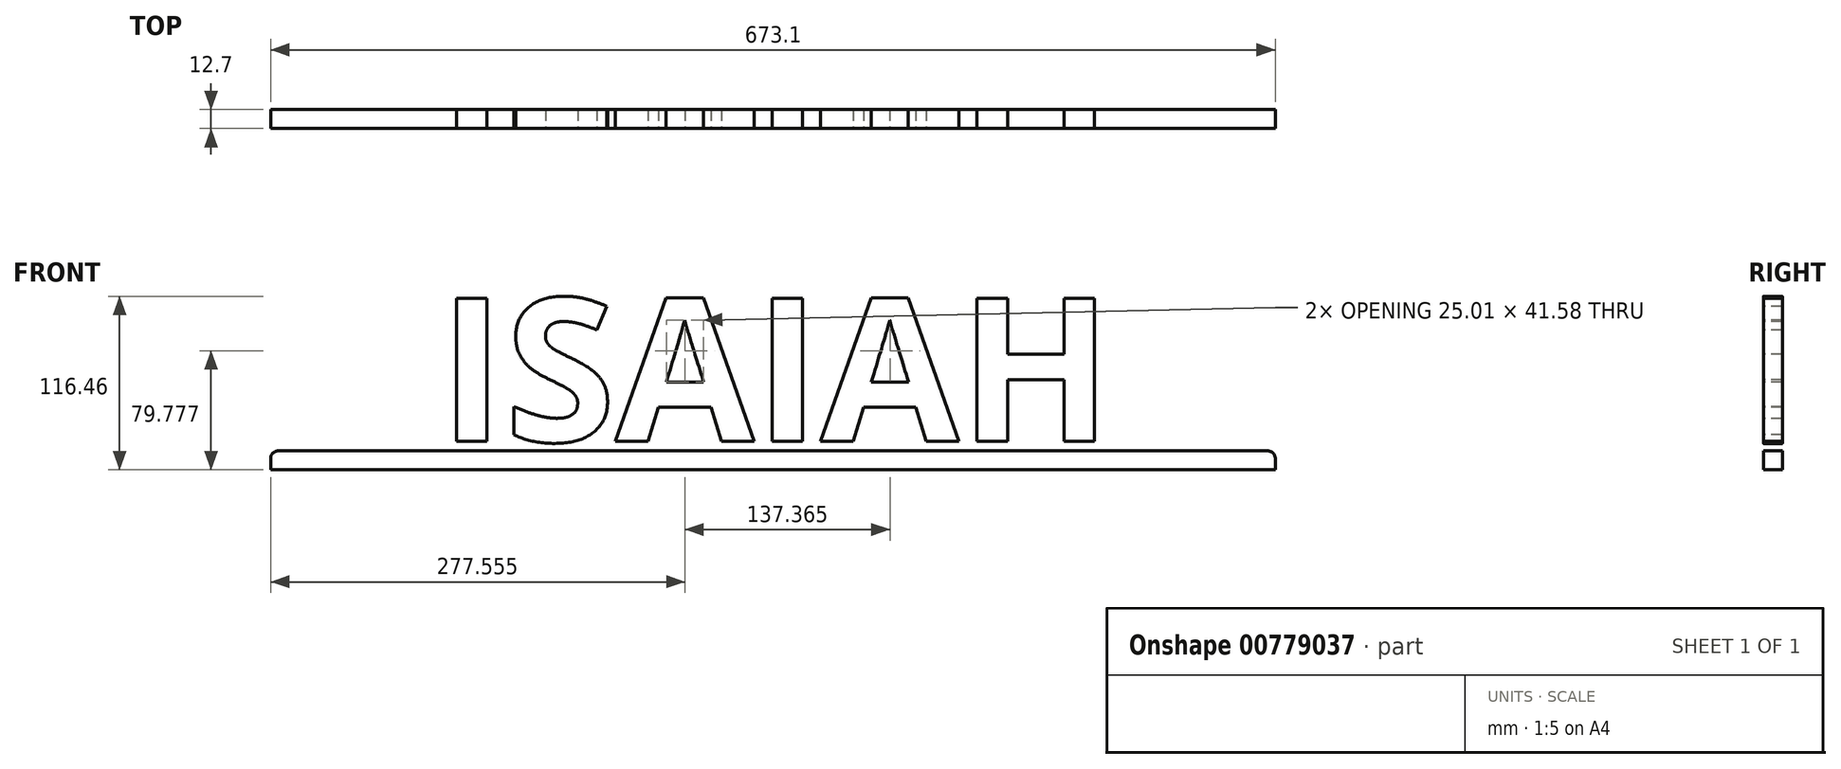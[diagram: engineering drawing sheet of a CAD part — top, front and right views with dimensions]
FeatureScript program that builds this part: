
annotation { "Feature Type Name" : "Feature", "Feature Type Description" : "" }
export const myFeature = defineFeature(function(context is Context, id is Id, definition is map)
    precondition{}
    {
        {
            var Q0;
            Q0=qCreatedBy(makeId("Front.planeOp"),FACE);
            var sketch = newSketch(context, id + "F0", { "sketchPlane" : qUnion([Q0])});
            skLineSegment(sketch, "E0.bottom", {"start": v(-336.55, -18.8) * mm, "end": v(336.55, -18.8) * mm});
            skLineSegment(sketch, "E0.top", {"start": v(-336.55, -31.5) * mm, "end": v(336.55, -31.5) * mm});
            skLineSegment(sketch, "E0.left", {"start": v(-336.55, -18.8) * mm, "end": v(-336.55, -31.5) * mm});
            skLineSegment(sketch, "E0.right", {"start": v(336.55, -18.8) * mm, "end": v(336.55, -31.5) * mm});
            skPoint(sketch, "E1", {"position": v(0, -18.8) * mm});
            skPoint(sketch, "E2", {"position": v(0, -31.5) * mm});
            skSolve(sketch);
        }
        {
            var Q0;
            Q0=makeQuery(id+"F0.imprint","IMPRINT",FACE,{"disambiguationData":[TD([[makeQuery(id+"F0.imprint","IMPRINT",EDGE,{"derivedFrom":sQuery(id+"F0.wireOp",EDGE,"E0.bottom")}),-1.0]])]});
            extrude(context, id + "F1", {"entities" : qUnion([Q0]), "depth" : 12.7 * mm, "offsetDistance" : 25.4 * mm});
        }
        {
            var Q0;
            Q0=makeQuery(id+"F1.opExtrude","CAP_FACE",FACE,{"disambiguationData":[OSD([sQuery(id+"F0.wireOp",EDGE,"E0.bottom"),sQuery(id+"F0.wireOp",EDGE,"E0.top"),sQuery(id+"F0.wireOp",EDGE,"E0.left"),sQuery(id+"F0.wireOp",EDGE,"E0.right")])],"isStart":false});
            var sketch = newSketch(context, id + "F2", { "sketchPlane" : qUnion([Q0])});
            skText(sketch, "E3", { "text": "ISAIAH", "fontName": "OpenSans-Bold.ttf"});
            const initialGuessF2  = {"E3": [-0.22417, -0.01245, 1, 0, 0.09686]};
            skSetInitialGuess(sketch, initialGuessF2);
            skSolve(sketch);
        }
        {
            var Q0;
            Q0=qSketchRegion(id+"F2",true);
            extrude(context, id + "F3", {"entities" : qUnion([Q0]), "operationType" : NewBodyOperationType.ADD, "depth" : -12.7 * mm, "offsetDistance" : 25.4 * mm});
        }
        {
            var Q0;
            Q0=makeQuery(id+"F1.opExtrude","SWEPT_EDGE",EDGE,{"disambiguationData":[OSD([sQuery(id+"F0.wireOp",EDGE,"E0.bottom"),sQuery(id+"F0.wireOp",EDGE,"E0.right")])]});
            var Q1;
            Q1=makeQuery(id+"F1.opExtrude","SWEPT_EDGE",EDGE,{"disambiguationData":[OSD([sQuery(id+"F0.wireOp",EDGE,"E0.bottom"),sQuery(id+"F0.wireOp",EDGE,"E0.left")])]});
            fillet(context, id + "F4", {"entities" : qUnion([Q0, Q1]), "radius" : 5.08 * mm, "tangentPropagation" : true, "allowEdgeOverflow" : false});
        }
    });
